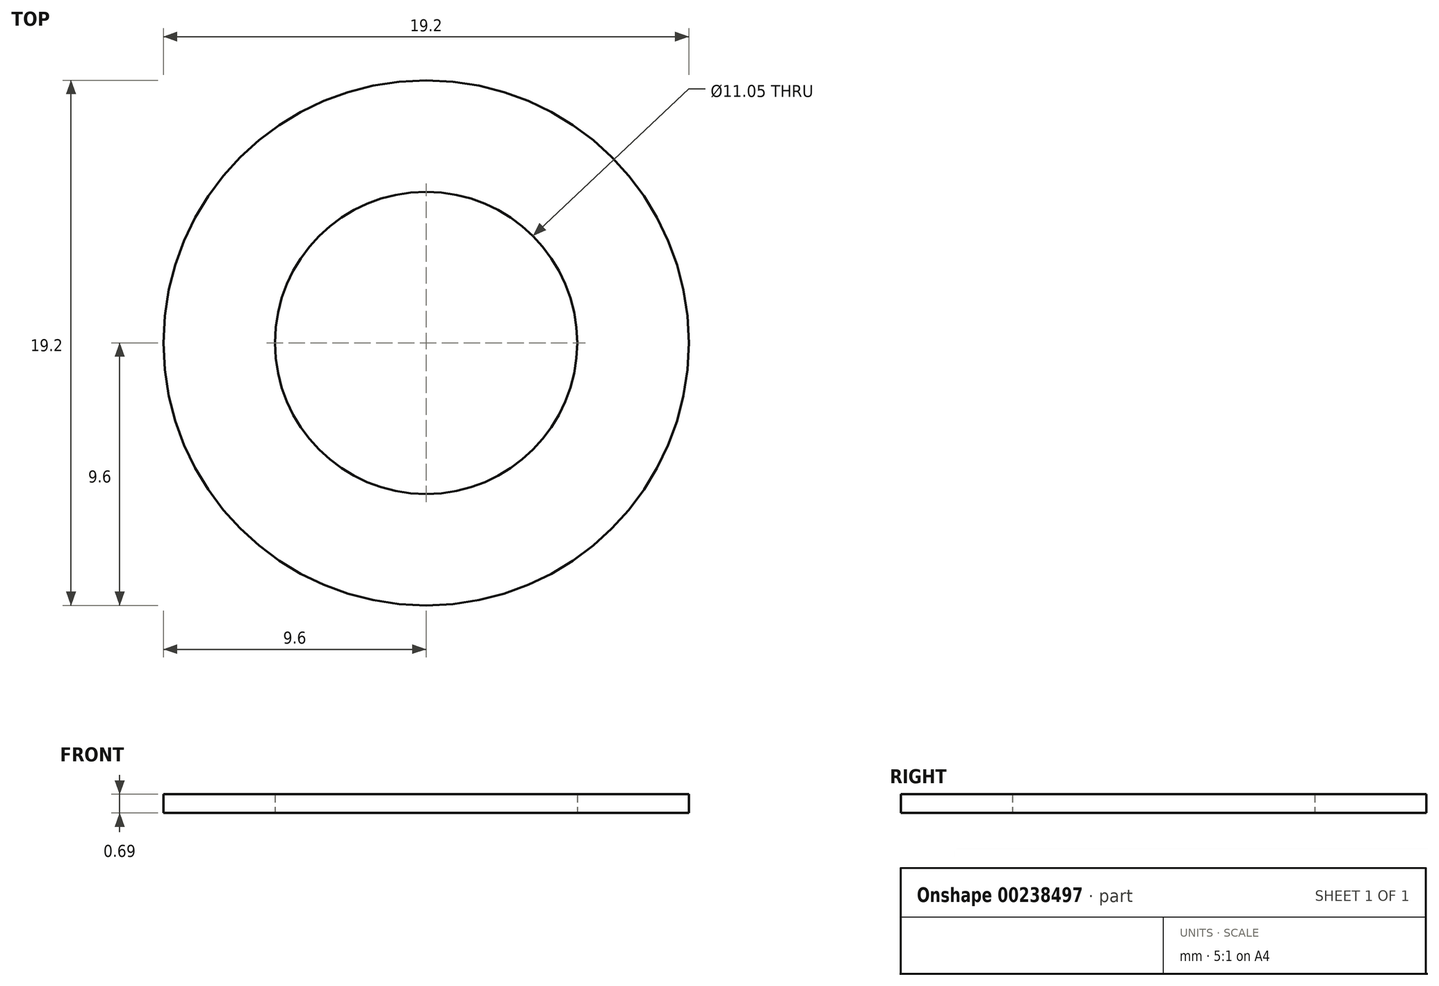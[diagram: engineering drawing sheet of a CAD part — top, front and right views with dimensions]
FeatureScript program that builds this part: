
annotation { "Feature Type Name" : "Feature", "Feature Type Description" : "" }
export const myFeature = defineFeature(function(context is Context, id is Id, definition is map)
    precondition{}
    {
        {
            var Q0;
            Q0=qCreatedBy(makeId("Top.planeOp"),FACE);
            var sketch = newSketch(context, id + "F0", { "sketchPlane" : qUnion([Q0])});
            skCircle(sketch, "E0", {"center": v(0, 0) * mm, "radius": 9.6 * mm});
            skCircle(sketch, "E1", {"center": v(0, 0) * mm, "radius": 5.52 * mm});
            skSolve(sketch);
        }
        {
            var Q0;
            Q0 = qSketchRegion(id + "F0", true);
            extrude(context, id + "F1", {"entities" : qUnion([Q0]), "depth" : 0.69 * mm});
        }
    });
